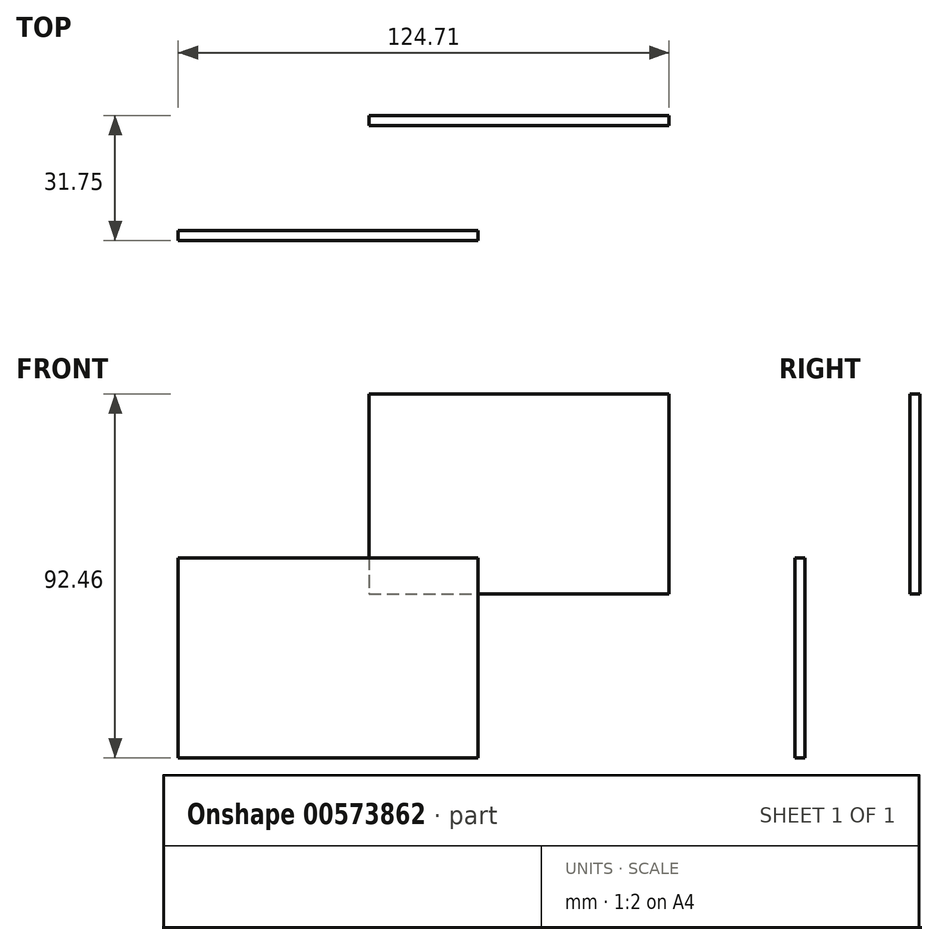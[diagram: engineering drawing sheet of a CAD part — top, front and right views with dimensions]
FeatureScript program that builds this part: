
annotation { "Feature Type Name" : "Feature", "Feature Type Description" : "" }
export const myFeature = defineFeature(function(context is Context, id is Id, definition is map)
    precondition{}
    {
        {
            var Q0;
            Q0=qCreatedBy(makeId("Front.planeOp"),FACE);
            var sketch = newSketch(context, id + "F0", { "sketchPlane" : qUnion([Q0])});
            skLineSegment(sketch, "E0.bottom", {"start": v(-40.4, 27.11) * mm, "end": v(35.8, 27.11) * mm});
            skLineSegment(sketch, "E0.top", {"start": v(-40.4, -23.69) * mm, "end": v(35.8, -23.69) * mm});
            skLineSegment(sketch, "E0.left", {"start": v(-40.4, 27.11) * mm, "end": v(-40.4, -23.69) * mm});
            skLineSegment(sketch, "E0.right", {"start": v(35.8, 27.11) * mm, "end": v(35.8, -23.69) * mm});
            skSolve(sketch);
        }
        {
            var Q0;
            Q0 = qSketchRegion(id + "F0", true);
            extrude(context, id + "F1", {"entities" : qUnion([Q0]), "depth" : 2.54 * mm, "offsetDistance" : 25.4 * mm});
        }
        {
            var Q0;
            Q0=makeQuery(id+"F1.opExtrude","SWEPT_BODY",BODY,{"disambiguationData":[OSD([sQuery(id+"F0.wireOp",EDGE,"E0.bottom"),sQuery(id+"F0.wireOp",EDGE,"E0.top"),sQuery(id+"F0.wireOp",EDGE,"E0.left"),sQuery(id+"F0.wireOp",EDGE,"E0.right")])]});
            transform(context, id + "F2", {"entities" : qUnion([Q0]), "transformType" : TransformType.TRANSLATION_3D, "dx" : 48.5 * mm, "dy" : 29.2 * mm, "dz" : 41.66 * mm, "makeCopy" : true});
        }
    });
